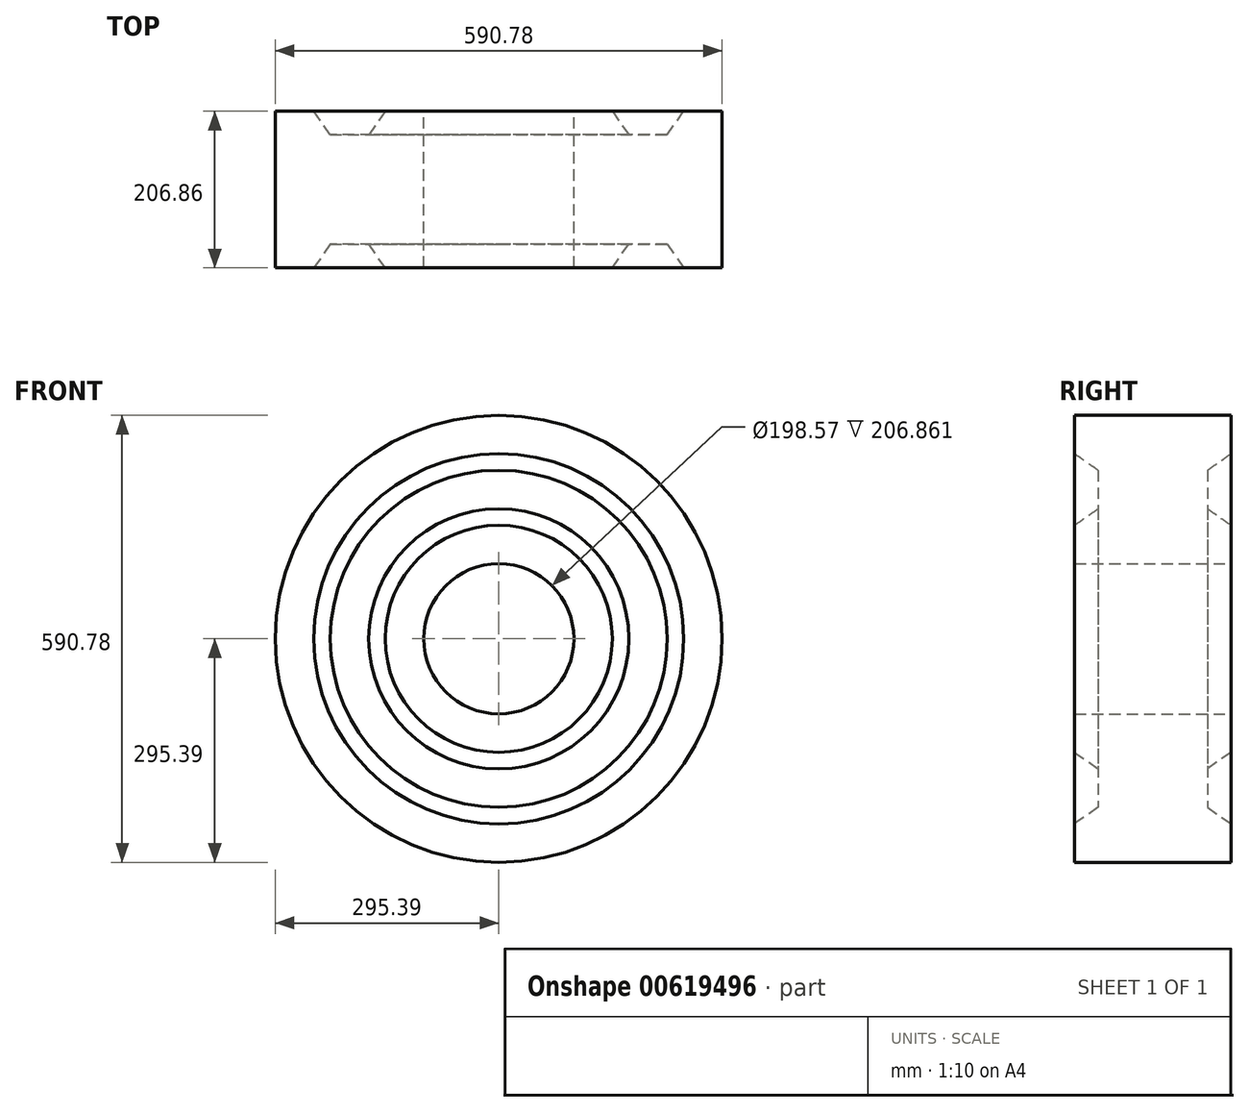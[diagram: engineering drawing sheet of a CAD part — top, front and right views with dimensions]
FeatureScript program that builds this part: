
annotation { "Feature Type Name" : "Feature", "Feature Type Description" : "" }
export const myFeature = defineFeature(function(context is Context, id is Id, definition is map)
    precondition{}
    {
        {
            var Q0;
            Q0=qCreatedBy(makeId("Right.planeOp"),FACE);
            var sketch = newSketch(context, id + "F0", { "sketchPlane" : qUnion([Q0])});
            skLineSegment(sketch, "E0", {"start": v(-103.43, 99.29) * mm, "end": v(103.43, 99.29) * mm});
            skLineSegment(sketch, "E1", {"start": v(103.43, 99.29) * mm, "end": v(103.43, 150.09) * mm});
            skLineSegment(sketch, "E2", {"start": v(103.43, 150.09) * mm, "end": v(72.22, 171.94) * mm});
            skLineSegment(sketch, "E3", {"start": v(72.22, 171.94) * mm, "end": v(72.22, 222.74) * mm});
            skLineSegment(sketch, "E4", {"start": v(72.22, 222.74) * mm, "end": v(103.43, 244.6) * mm});
            skLineSegment(sketch, "E5", {"start": v(103.43, 244.6) * mm, "end": v(103.43, 295.4) * mm});
            skLineSegment(sketch, "E6", {"start": v(103.43, 295.4) * mm, "end": v(-103.43, 295.4) * mm});
            skLineSegment(sketch, "E7", {"start": v(-103.43, 295.4) * mm, "end": v(-103.43, 244.6) * mm});
            skLineSegment(sketch, "E8", {"start": v(-103.43, 244.6) * mm, "end": v(-72.22, 222.74) * mm});
            skLineSegment(sketch, "E9", {"start": v(-72.22, 222.74) * mm, "end": v(-72.22, 171.94) * mm});
            skLineSegment(sketch, "E10", {"start": v(-72.22, 171.94) * mm, "end": v(-103.43, 150.09) * mm});
            skLineSegment(sketch, "E11", {"start": v(-103.43, 150.09) * mm, "end": v(-103.43, 99.29) * mm});
            skLineSegment(sketch, "E12", {"start": v(0, 0) * mm, "end": v(-393.13, 0) * mm, "construction": true});
            skLineSegment(sketch, "E13", {"start": v(0, 0) * mm, "end": v(0, 364.29) * mm, "construction": true});
            skSolve(sketch);
        }
        {
            var Q0;
            Q0=makeQuery(id+"F0.imprint","IMPRINT",FACE,{"disambiguationData":[TD([[makeQuery(id+"F0.imprint","IMPRINT",EDGE,{"derivedFrom":sQuery(id+"F0.wireOp",EDGE,"E0")}),1.0]])]});
            var Q1;
            Q1=sQuery(id+"F0.wireOp",EDGE,"E12");
            revolve(context, id + "F1", {"entities" : qUnion([Q0]), "axis" : qUnion([Q1]), "revolveType" : RevolveType.FULL});
        }
    });
